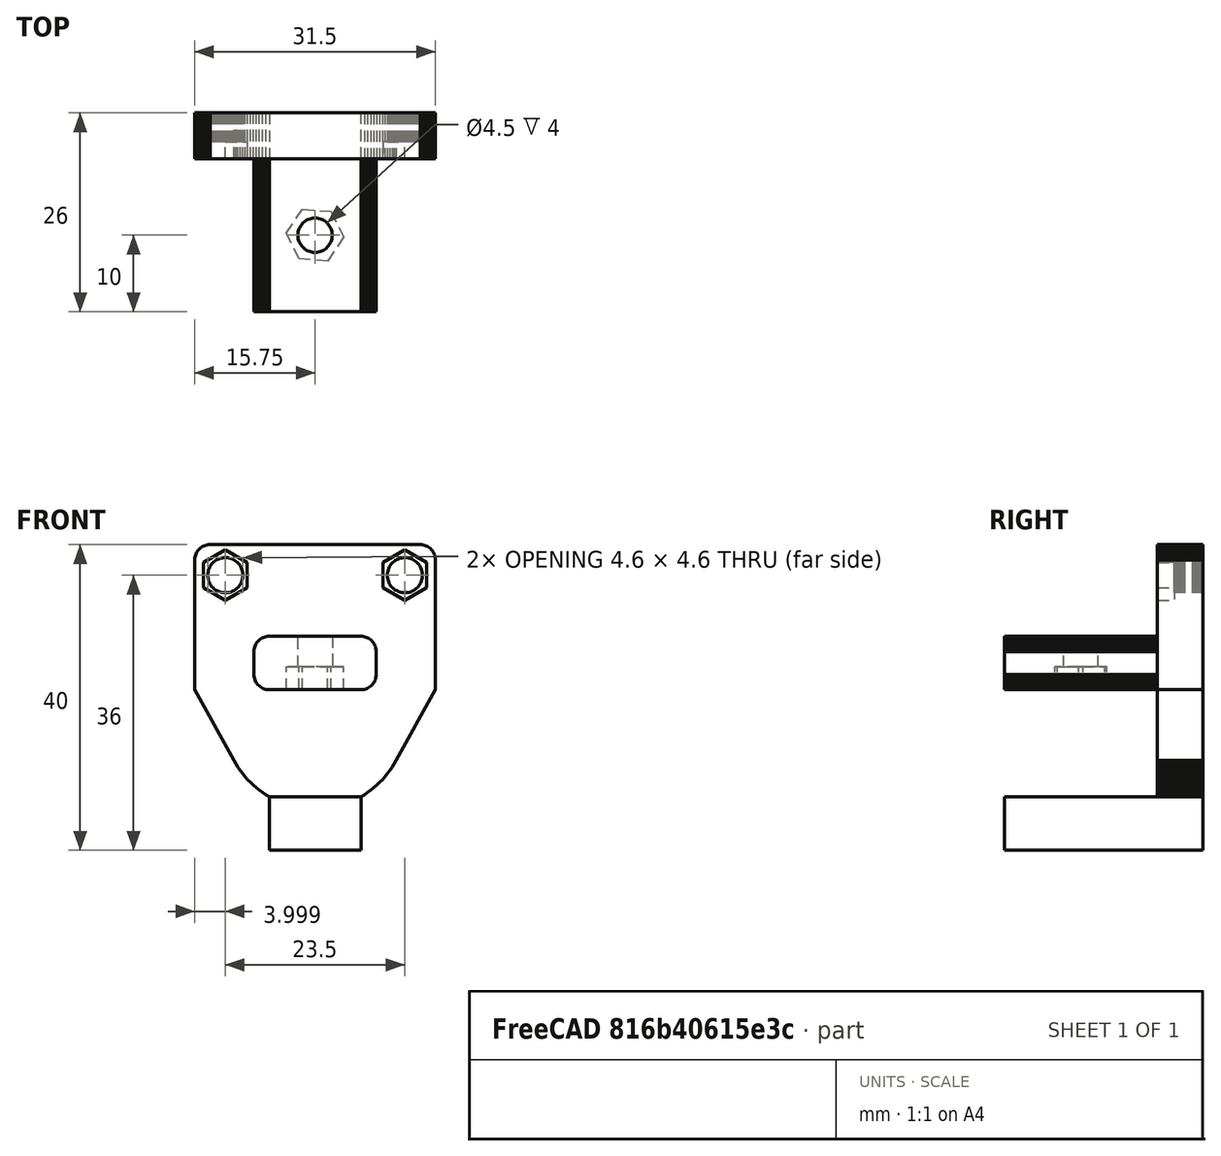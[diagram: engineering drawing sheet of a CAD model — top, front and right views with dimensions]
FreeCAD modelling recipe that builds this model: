
FCSTD DOCUMENT  (FreeCAD 1.2R20260113 (Git shallow))
Label: kusba-mount-remix
License: All rights reserved
LicenseURL: http://en.wikipedia.org/wiki/All_rights_reserved
objects: Sketcher::SketchObject×4, Part::Feature×2, PartDesign::Pad×2, PartDesign::Pocket×2, Mesh::Feature×1, Part::Refine×1, App::Point×1, PartDesign::FeatureBase×1, PartDesign::Body×1
note: 26 computed .brp shape members not serialized (recipe doc carries the construction recipe); baked Part::Feature solids carry a one-line shape summary decoded from their .brp

FEATURE [Mesh::Feature] kusb_ender3_x_y_mount  label="kusb-ender3-x-y-mount"
FEATURE [Part::Feature] kusb_ender3_x_y_mount001
  shape: bbox 31.5 x 26 x 40 mm, 1856 faces, 0 solids (baked)
FEATURE [Part::Refine] kusb_ender3_x_y_mount002
  Source = -> kusb_ender3_x_y_mount001
FEATURE [Part::Feature] kusb_ender3_x_y_mount002_solid  label="kusb_ender3_x_y_mount002 (Solid)"
  shape: bbox 31.5 x 26 x 40 mm, 406 faces (baked)
FEATURE [App::Point] Origin001
  Role = Origin
FEATURE [PartDesign::FeatureBase] BaseFeature
  BaseFeature = -> kusb_ender3_x_y_mount002_solid
  Suppressed = false
FEATURE [Sketcher::SketchObject] Sketch
  ArcFitTolerance = 1e-06
  AttachmentSupport = -> [BaseFeature]
  ExternalGeometry = -> [BaseFeature]
  ExternalTypes = [0,0,0,0,0,0]
  FullyConstrained = true
  MakeInternals = false
  MapMode = 5
  Placement = pos=(0,0,-12.7999) rot=(1,0,0;3.14159rad)
FEATURE [PartDesign::Pad] Pad
  BaseFeature = -> BaseFeature
  Direction = (0,0,-1)
  Length = 10
  Length2 = 10
  Profile = -> Sketch
  ReferenceAxis = -> Sketch [N_Axis]
  Refine = true
  SideType = 0
  Suppressed = false
  Type = 3
  Type2 = 0
  UpToFace = -> BaseFeature [Face136]
FEATURE [Sketcher::SketchObject] Sketch001
  ArcFitTolerance = 1e-06
  AttachmentSupport = -> [Pad]
  ExternalGeometry = -> [Pad]
  ExternalTypes = [0,0,0]
  FullyConstrained = true
  MakeInternals = false
  MapMode = 5
  Placement = pos=(0,0,-12.7999) rot=(0,0,1;0rad)
  sketch-geometry (1):
    g0: Circle CenterX=11.75 CenterY=-10 CenterZ=0 NormalX=0 NormalY=0 NormalZ=1 AngleXU=0 Radius=2.3
  constraints (3):
    c: PointOnObject(g-3,g0)
    c: PointOnObject(g-4,g0)
    c: PointOnObject(g-5,g0)
FEATURE [PartDesign::Pad] Pad001
  BaseFeature = -> Pad
  Direction = (0,0,1)
  Length = 10
  Length2 = 10
  Profile = -> Sketch001
  ReferenceAxis = -> Sketch001 [N_Axis]
  Refine = true
  SideType = 0
  Suppressed = false
  Type = 3
  Type2 = 0
  UpToFace = -> Pad [Face195]
FEATURE [Sketcher::SketchObject] Sketch002
  ArcFitTolerance = 1e-06
  AttachmentSupport = -> [Pad001]
  ExternalGeometry = -> [Pad001]
  ExternalTypes = [0,0]
  FullyConstrained = true
  MakeInternals = false
  MapMode = 5
  Placement = pos=(0,0,-7.99994) rot=(0,0,1;0rad)
  sketch-geometry (1):
    g0: Circle CenterX=11.75 CenterY=-10 CenterZ=0 NormalX=0 NormalY=0 NormalZ=1 AngleXU=0 Radius=2.25
  constraints (2):
    c: Diameter(g0) = 4.5
    c: Symmetric(g-4,g-3,g0)
FEATURE [PartDesign::Pocket] Pocket
  BaseFeature = -> Pad001
  Direction = (0,0,-1)
  Length = 5
  Length2 = 5
  Profile = -> Sketch002
  ReferenceAxis = -> Sketch002 [N_Axis]
  SideType = 0
  Suppressed = false
  Type = 2
  Type2 = 0
FEATURE [Sketcher::SketchObject] Sketch003
  ArcFitTolerance = 1e-06
  AttachmentSupport = -> [Pocket]
  ExternalGeometry = -> [Pocket]
  ExternalTypes = [0]
  FullyConstrained = false
  MakeInternals = false
  MapMode = 5
  Placement = pos=(0,0,-14.9999) rot=(1,0,0;3.14159rad)
  sketch-geometry (7):
    g0: LineSegment StartX=15.4939 StartY=10.2579 StartZ=0 EndX=13.3986 EndY=13.3713 EndZ=0
    g1: LineSegment StartX=13.3986 StartY=13.3713 StartZ=0 EndX=9.65467 EndY=13.1133 EndZ=0
    g2: LineSegment StartX=9.65467 StartY=13.1133 StartZ=0 EndX=8.0061 EndY=9.74207 EndZ=0
    g3: LineSegment StartX=8.0061 StartY=9.74207 StartZ=0 EndX=10.1014 EndY=6.62872 EndZ=0
    g4: LineSegment StartX=10.1014 StartY=6.62872 StartZ=0 EndX=13.8453 EndY=6.88665 EndZ=0
    g5: LineSegment StartX=13.8453 StartY=6.88665 StartZ=0 EndX=15.4939 EndY=10.2579 EndZ=0
    g6: Circle [constr] CenterX=11.75 CenterY=10 CenterZ=0 NormalX=0 NormalY=0 NormalZ=1 AngleXU=0 Radius=3.75278
  constraints (15):
    c: Coincident(g0,g1)
    c: Coincident(g1,g2)
    c: Coincident(g2,g3)
    c: Coincident(g3,g4)
    c: Coincident(g4,g5)
    c: Coincident(g5,g0)
    c: Equal(g0, g1-g5) x5
    c: PointOnObject(g0,g6)
    c: PointOnObject(g1,g6)
    c: PointOnObject(g2,g6)
    c: PointOnObject(g3,g6)
    c: PointOnObject(g4,g6)
    c: PointOnObject(g5,g6)
    c: Coincident(g6,g-3)
    c: Distance(g5,g2) = 6.5
FEATURE [PartDesign::Pocket] Pocket001
  BaseFeature = -> Pocket
  Direction = (0,0,1)
  Length = 3
  Length2 = 5
  Profile = -> Sketch003
  ReferenceAxis = -> Sketch003 [N_Axis]
  SideType = 0
  Suppressed = false
  Type = 0
  Type2 = 0
FEATURE [PartDesign::Body] Body
  AllowCompound = false
  BaseFeature = -> kusb_ender3_x_y_mount002_solid
  Group = -> [BaseFeature,Sketch,Pad,Sketch001,Pad001,Sketch002,Pocket,Sketch003,Pocket001]
  Origin = -> Origin
  Tip = -> Pocket001
